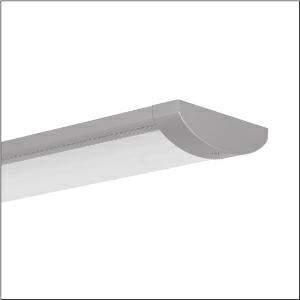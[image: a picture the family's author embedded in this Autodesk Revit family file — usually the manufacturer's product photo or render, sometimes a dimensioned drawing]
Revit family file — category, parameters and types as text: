
# Revit family: tv_20_5xa861d2n0a
name_source: partatom
category: Lighting Fixtures
units: mm (PartAtom-declared; Revit-internal decimal feet)

## family parameters
Cut with Voids When Loaded = No
Host = Face
Light Source = No
Part Type = Normal
Room Calculation Point = No
Round Connector Dimension = Use Diameter
Shared = No

## types (1)
- TV 20 (1 x LED 4000K / CRI = 80 (unbekannt), 2130 lm, 4000K)
    Apparent Load = 21 VA
    CIE Flux Codes = 48 78 95 99 100
    Color Rendering = 80
    Color Temperature = 4000K
    Default Elevation = 1800 mm
    Description = TV 20, vandal-proof luminaire, primary light control with specular reflector, of aluminium, matt, primary optical cover: enclosure, of PC, frosted, light emission: direct distribution, primary light characteristic: symmetric, installation type: surface-mounted, LED, rated luminous flux: 2.130lm, luminous efficacy: 101lm/W, light colour: 840, colour temperature: 4000K, control gear: ECG DALI, mains connection: 230V, AC, 50Hz, rated input power: 21W, luminaire housing, of aluminium, coated, Siteco® metallic grey (DB 702S), with wall and ceiling fixing element, length: 705mm, width: 260mm, height: 70mm, protection rating (complete): IP65, insulation class (complete): insulation class I (protective earthing), certification: CE, protection symbol: F, impact resistance: 2x IK10, standard: EN 60598, packaging unit: 1 piece
    Height = 70 mm
    Lamp = 1 x LED 4000K / CRI >= 80 (unbekannt)
    Lamp Light Flux = 2130 lm
    Lamp count = 1
    Length = 705 mm
    Luminous efficacy = 101 lm/W
    Manufacturer = Siteco
    ModVariant = No
    Model = 5XA861D2N0A
    Mounting Place = Ceiling
    Mounting Type = Surface mounted
    Number of Poles = 1
    OnlyDefault = Yes
    Power Factor = 1
    Product Name = TV 20
    Product group = vandal-proof luminaire
    ProductGroupID = 307
    Protection Class = Protection class I
    Protection Degree = IP 65
    RLX_Detail_Level = 1
    RLX_Emergency_Light_Flux = 0 lm
    RLX_Emergency_Type = 0
    RLX_Emergency_Type_DB = No
    RlxData = <blob elided: 34193 chars, md5=7f30b0f3>
    Socket = socket
    Standby Power = 0 W
    System Light Flux = 2130 lm
    System Power = 21 W
    Type Comments = Product without accessories
    Type Image = l_1004809.jpg
    URL = http://relux.com
    VarID = ---
    Voltage = 0 V
    Weight = 0.00 kg
    Width = 260 mm

## geometry (parser evidence)
native form markers: Blend x4, Sweep x9
no freeform markers — native parametric forms only
